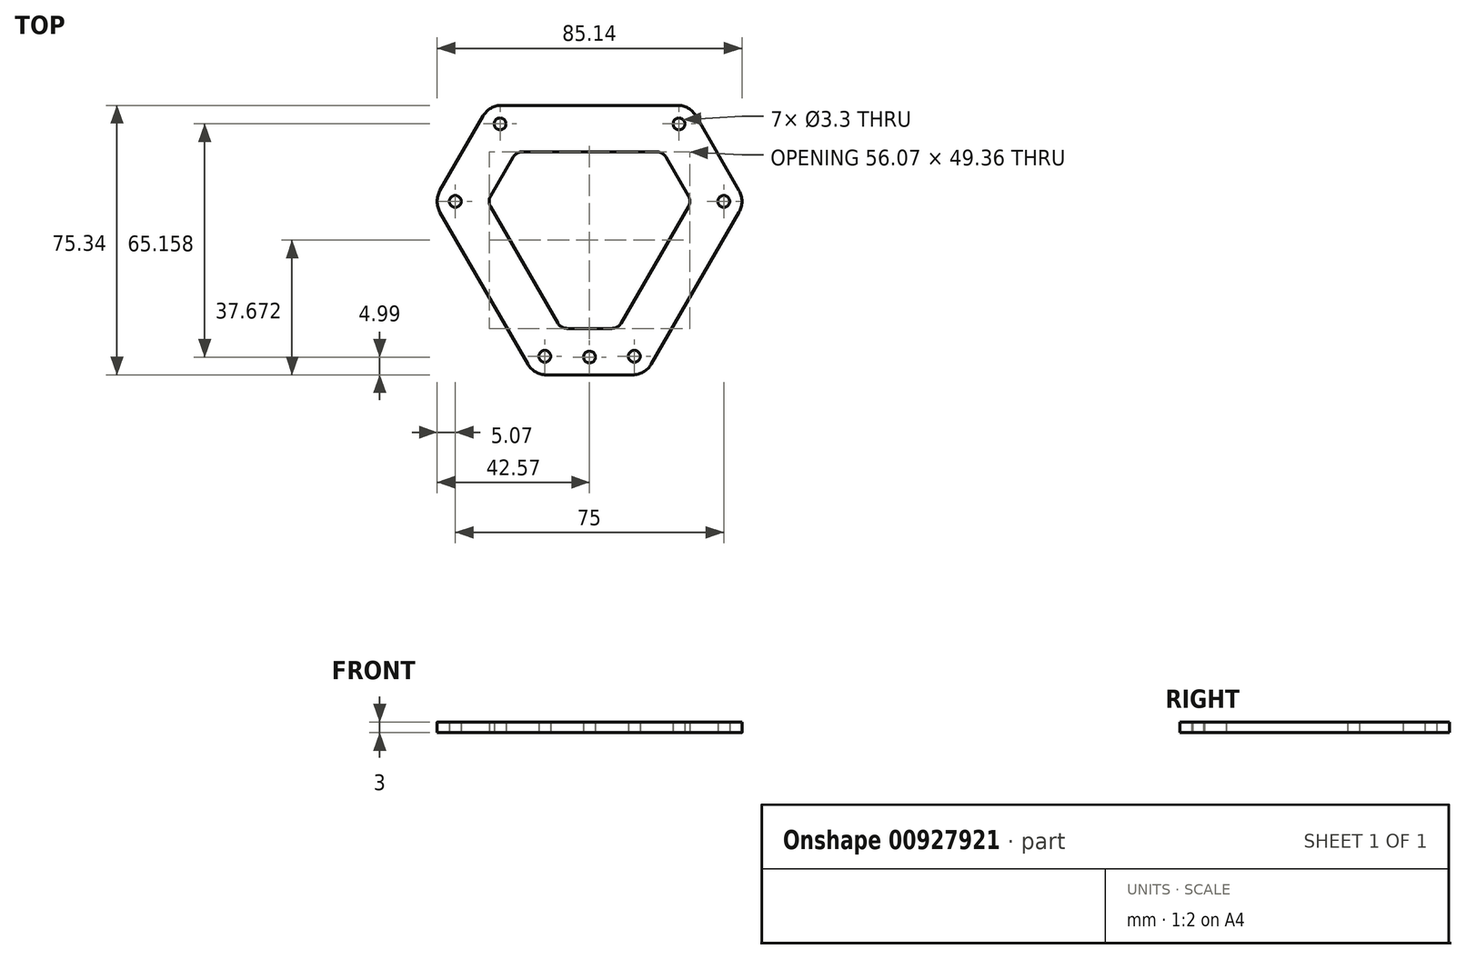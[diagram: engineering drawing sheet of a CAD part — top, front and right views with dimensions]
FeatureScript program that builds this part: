
annotation { "Feature Type Name" : "Feature", "Feature Type Description" : "" }
export const myFeature = defineFeature(function(context is Context, id is Id, definition is map)
    precondition{}
    {
        {
            var Q0;
            Q0=qCreatedBy(makeId("Top.planeOp"),FACE);
            var sketch = newSketch(context, id + "F0", { "sketchPlane" : qUnion([Q0])});
            skCircle(sketch, "E0.cCircle", {"center": v(0, 0) * mm, "radius": 28.87 * mm, "construction": true});
            skLineSegment(sketch, "E0.0", {"start": v(-25, 28.87) * mm, "end": v(25, 28.87) * mm, "construction": true});
            skLineSegment(sketch, "E0.1", {"start": v(37.5, 7.22) * mm, "end": v(12.5, -36.08) * mm, "construction": true});
            skLineSegment(sketch, "E0.2", {"start": v(-12.5, -36.08) * mm, "end": v(-37.5, 7.22) * mm, "construction": true});
            skPoint(sketch, "E0.0.midPoint", {"position": v(0, 28.87) * mm});
            skLineSegment(sketch, "E1", {"start": v(-12.5, -36.08) * mm, "end": v(12.5, -36.08) * mm, "construction": true});
            skLineSegment(sketch, "E2", {"start": v(48.86, 7.22) * mm, "end": v(-54.17, 7.22) * mm, "construction": true});
            skLineSegment(sketch, "E3", {"start": v(-19.55, -48.3) * mm, "end": v(30.95, 39.17) * mm, "construction": true});
            skLineSegment(sketch, "E4", {"start": v(21.82, -52.23) * mm, "end": v(-31.38, 39.91) * mm, "construction": true});
            skLineSegment(sketch, "E5", {"start": v(-25, 28.87) * mm, "end": v(-37.5, 7.22) * mm, "construction": true});
            skLineSegment(sketch, "E6", {"start": v(25, 28.87) * mm, "end": v(37.5, 7.22) * mm, "construction": true});
            skPoint(sketch, "E7.orphan", {"position": v(0, -57.74) * mm});
            skPoint(sketch, "E8.orphan", {"position": v(50, 28.87) * mm});
            skPoint(sketch, "E9.orphan", {"position": v(-50, 28.87) * mm});
            skCircle(sketch, "E10", {"center": v(-25, 28.87) * mm, "radius": 1.65 * mm});
            skCircle(sketch, "E11", {"center": v(25, 28.87) * mm, "radius": 1.65 * mm});
            skCircle(sketch, "E12", {"center": v(37.5, 7.22) * mm, "radius": 1.65 * mm});
            skCircle(sketch, "E13", {"center": v(12.5, -36.08) * mm, "radius": 1.65 * mm});
            skCircle(sketch, "E14", {"center": v(-12.5, -36.08) * mm, "radius": 1.65 * mm});
            skCircle(sketch, "E15", {"center": v(-37.5, 7.22) * mm, "radius": 1.65 * mm});
            skLineSegment(sketch, "E16", {"start": v(-29.73, 31.06) * mm, "end": v(-41.77, 10.22) * mm});
            skLineSegment(sketch, "E17", {"start": v(-41.77, 4.22) * mm, "end": v(-17.23, -38.28) * mm});
            skLineSegment(sketch, "E18", {"start": v(-12.04, -41.28) * mm, "end": v(12.04, -41.28) * mm});
            skLineSegment(sketch, "E19", {"start": v(17.23, -38.28) * mm, "end": v(41.77, 4.22) * mm});
            skLineSegment(sketch, "E20", {"start": v(41.77, 10.22) * mm, "end": v(29.73, 31.06) * mm});
            skLineSegment(sketch, "E21", {"start": v(24.54, 34.06) * mm, "end": v(-24.54, 34.06) * mm});
            skPoint(sketch, "E22.visualSharp", {"position": v(-28, 34.06) * mm});
            skArc(sketch, "E22.filletArc", {"start": v(-24.54, 34.06) * mm, "mid": v(-27.54, 33.26) * mm, "end": v(-29.73, 31.06) * mm});
            skPoint(sketch, "E23.visualSharp", {"position": v(-43.5, 7.22) * mm});
            skArc(sketch, "E23.filletArc", {"start": v(-41.77, 10.22) * mm, "mid": v(-42.57, 7.22) * mm, "end": v(-41.77, 4.22) * mm});
            skPoint(sketch, "E24.visualSharp", {"position": v(-15.5, -41.28) * mm});
            skArc(sketch, "E24.filletArc", {"start": v(-17.23, -38.28) * mm, "mid": v(-15.04, -40.48) * mm, "end": v(-12.04, -41.28) * mm});
            skPoint(sketch, "E25.visualSharp", {"position": v(15.5, -41.28) * mm});
            skArc(sketch, "E25.filletArc", {"start": v(12.04, -41.28) * mm, "mid": v(15.04, -40.48) * mm, "end": v(17.23, -38.28) * mm});
            skPoint(sketch, "E26.visualSharp", {"position": v(43.5, 7.22) * mm});
            skArc(sketch, "E26.filletArc", {"start": v(41.77, 4.22) * mm, "mid": v(42.57, 7.22) * mm, "end": v(41.77, 10.22) * mm});
            skPoint(sketch, "E27.visualSharp", {"position": v(28, 34.06) * mm});
            skArc(sketch, "E27.filletArc", {"start": v(29.73, 31.06) * mm, "mid": v(27.54, 33.26) * mm, "end": v(24.54, 34.06) * mm});
            skLineSegment(sketch, "E28", {"start": v(-6.27, -28.3) * mm, "end": v(6.27, -28.3) * mm});
            skLineSegment(sketch, "E29", {"start": v(8.87, -26.8) * mm, "end": v(27.63, 5.72) * mm});
            skLineSegment(sketch, "E30", {"start": v(27.63, 8.72) * mm, "end": v(21.37, 19.57) * mm});
            skLineSegment(sketch, "E31", {"start": v(18.77, 21.07) * mm, "end": v(-18.77, 21.07) * mm});
            skLineSegment(sketch, "E32", {"start": v(-21.37, 19.57) * mm, "end": v(-27.63, 8.72) * mm});
            skLineSegment(sketch, "E33", {"start": v(-27.63, 5.72) * mm, "end": v(-8.87, -26.8) * mm});
            skPoint(sketch, "E34.visualSharp", {"position": v(-20.5, 21.07) * mm});
            skArc(sketch, "E34.filletArc", {"start": v(-18.77, 21.07) * mm, "mid": v(-20.27, 20.67) * mm, "end": v(-21.37, 19.57) * mm});
            skPoint(sketch, "E35.visualSharp", {"position": v(-28.5, 7.22) * mm});
            skArc(sketch, "E35.filletArc", {"start": v(-27.63, 8.72) * mm, "mid": v(-28.04, 7.22) * mm, "end": v(-27.63, 5.72) * mm});
            skPoint(sketch, "E36.visualSharp", {"position": v(-8, -28.3) * mm});
            skArc(sketch, "E36.filletArc", {"start": v(-8.87, -26.8) * mm, "mid": v(-7.77, -27.89) * mm, "end": v(-6.27, -28.3) * mm});
            skPoint(sketch, "E37.visualSharp", {"position": v(8, -28.3) * mm});
            skArc(sketch, "E37.filletArc", {"start": v(6.27, -28.3) * mm, "mid": v(7.77, -27.89) * mm, "end": v(8.87, -26.8) * mm});
            skPoint(sketch, "E38.visualSharp", {"position": v(28.5, 7.22) * mm});
            skArc(sketch, "E38.filletArc", {"start": v(27.63, 5.72) * mm, "mid": v(28.04, 7.22) * mm, "end": v(27.63, 8.72) * mm});
            skPoint(sketch, "E39.visualSharp", {"position": v(20.5, 21.07) * mm});
            skArc(sketch, "E39.filletArc", {"start": v(21.37, 19.57) * mm, "mid": v(20.27, 20.67) * mm, "end": v(18.77, 21.07) * mm});
            skCircle(sketch, "E40", {"center": v(0, -36.3) * mm, "radius": 1.65 * mm});
            skSolve(sketch);
        }
        {
            var Q0;
            Q0 = qSketchRegion(id + "F0", true);
            extrude(context, id + "F1", {"entities" : qUnion([Q0]), "depth" : 3 * mm, "offsetDistance" : 25 * mm});
        }
    });
